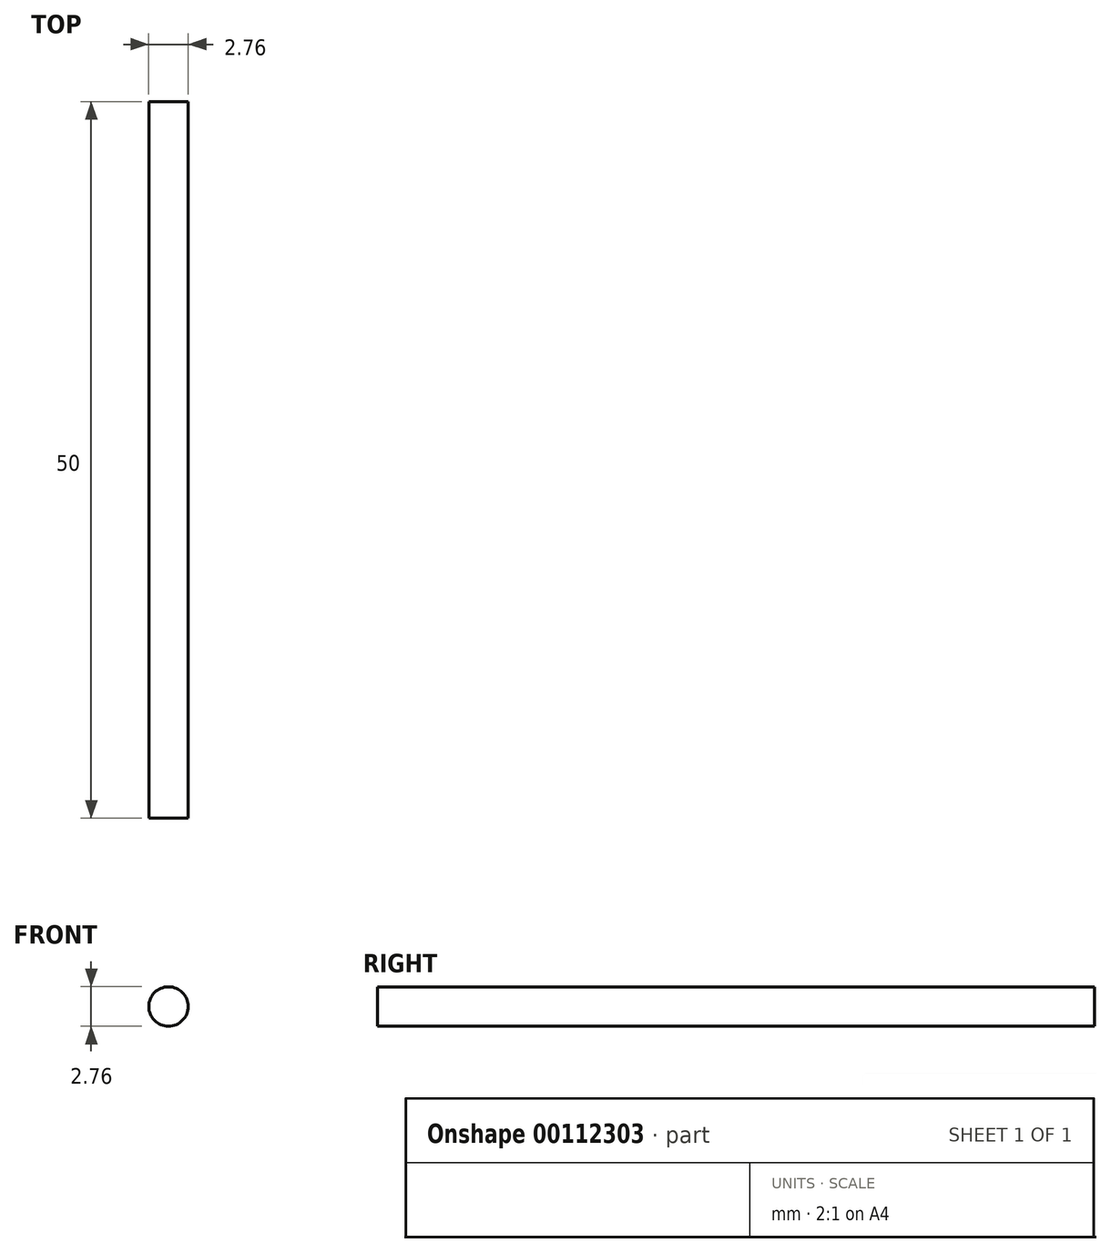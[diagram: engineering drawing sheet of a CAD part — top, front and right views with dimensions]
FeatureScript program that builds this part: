
annotation { "Feature Type Name" : "Feature", "Feature Type Description" : "" }
export const myFeature = defineFeature(function(context is Context, id is Id, definition is map)
    precondition{}
    {
        {
            var Q0;
            Q0=qCreatedBy(makeId("Front.planeOp"),FACE);
            var sketch = newSketch(context, id + "F0", { "sketchPlane" : qUnion([Q0])});
            skCircle(sketch, "E0", {"center": v(0, 0) * mm, "radius": 1.38 * mm});
            skSolve(sketch);
        }
        {
            var Q0;
            Q0=qSketchRegion(id+"F0",true);
            extrude(context, id + "F1", {"entities" : qUnion([Q0]), "depth" : 50 * mm});
        }
    });
